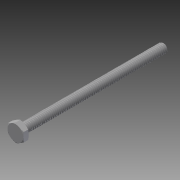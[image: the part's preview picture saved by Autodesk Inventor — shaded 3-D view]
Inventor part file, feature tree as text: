
AUTODESK INVENTOR PART (.ipt)
format: ipt  version: 2014 SP1 (Build 180222100, 222)  size: 1,436,672 bytes
history: native  units: in
note: dims shown in document units (in); Inventor stores cm internally (conversion verified against a paired STEP export)
features: extrude x1, other x1, imported_body x1
ambient origin geometry x8: Origin, YZ Plane, XZ Plane, XY Plane, X Axis, Y Axis, Z Axis, Center Point
bodies: Body1 (feature_tree)
feature tree (3):
  extrude  "Extrude14"  [1 undecoded]
  other  "92620A5551"
  imported_body  "Base1"
note: 1 required parameter value undecoded (feature->parameter linkage not recoverable at this tier; creation-order binding heuristic only, values carry confidence <= 0.55)
